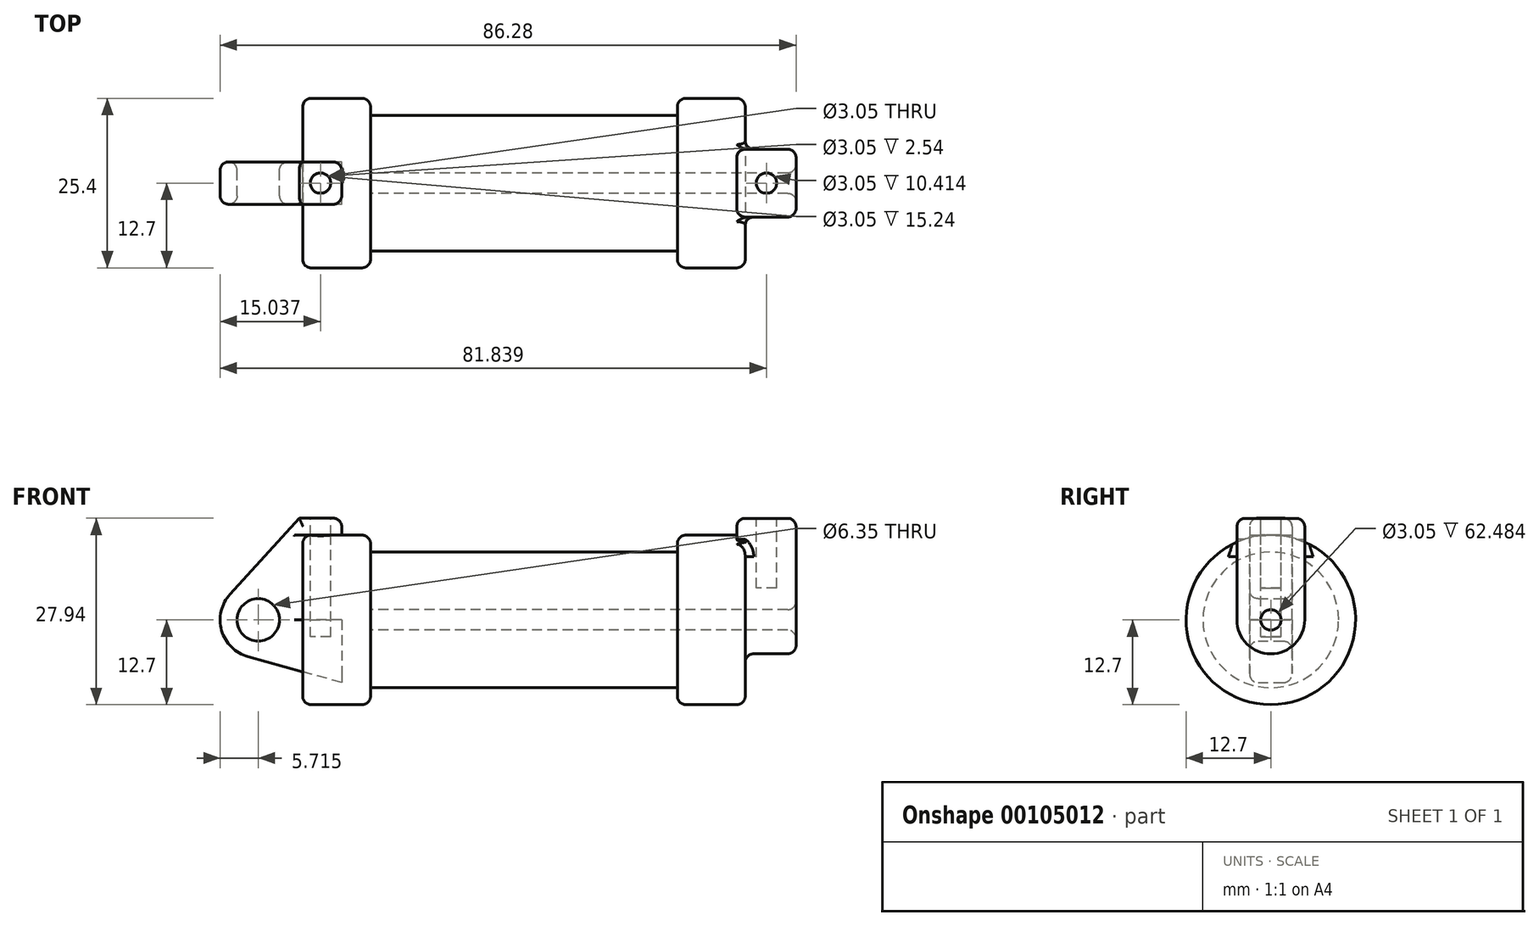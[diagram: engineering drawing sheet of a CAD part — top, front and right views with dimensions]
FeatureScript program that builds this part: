
annotation { "Feature Type Name" : "Feature", "Feature Type Description" : "" }
export const myFeature = defineFeature(function(context is Context, id is Id, definition is map)
    precondition{}
    {
        {
            var Q0;
            Q0=qCreatedBy(makeId("Front.planeOp"),FACE);
            var sketch = newSketch(context, id + "F0", { "sketchPlane" : qUnion([Q0])});
            skLineSegment(sketch, "E0", {"start": v(0, 0) * mm, "end": v(0, 12.7) * mm});
            skLineSegment(sketch, "E1", {"start": v(0, 12.7) * mm, "end": v(10.16, 12.7) * mm});
            skLineSegment(sketch, "E2", {"start": v(10.16, 12.7) * mm, "end": v(10.16, 10.16) * mm});
            skLineSegment(sketch, "E3", {"start": v(10.16, 10.16) * mm, "end": v(56.13, 10.16) * mm});
            skLineSegment(sketch, "E4", {"start": v(56.13, 10.16) * mm, "end": v(56.13, 12.7) * mm});
            skLineSegment(sketch, "E5", {"start": v(56.13, 12.7) * mm, "end": v(66.3, 12.7) * mm});
            skLineSegment(sketch, "E6", {"start": v(66.3, 12.7) * mm, "end": v(66.3, 0) * mm});
            skLineSegment(sketch, "E7", {"start": v(66.3, 0) * mm, "end": v(0, 0) * mm});
            skLineSegment(sketch, "E8", {"start": v(5.84, 15.24) * mm, "end": v(-0.5, 15.24) * mm});
            skLineSegment(sketch, "E9", {"start": v(-0.5, 15.24) * mm, "end": v(-10.88, 3.85) * mm});
            skLineSegment(sketch, "E10", {"start": v(0, 0) * mm, "end": v(-6.65, 0) * mm});
            skCircle(sketch, "E11", {"center": v(-6.65, 0) * mm, "radius": 5.72 * mm});
            skCircle(sketch, "E12", {"center": v(-6.65, 0) * mm, "radius": 3.18 * mm});
            skLineSegment(sketch, "E13", {"start": v(5.84, 15.24) * mm, "end": v(5.84, -9.4) * mm});
            skLineSegment(sketch, "E14", {"start": v(5.84, -9.4) * mm, "end": v(-8.18, -5.5) * mm});
            skSolve(sketch);
        }
        {
            var Q0;
            {var subQ0=sQuery(id+"F0.wireOp",EDGE,"E0");Q0=makeQuery(id+"F0.imprint","IMPRINT",FACE,{"disambiguationData":[TD([[makeQuery(id+"F0.imprint","IMPRINT",EDGE,{"derivedFrom":subQ0}),-1.0]])]});}
            var Q1;
            {var subQ0=sQuery(id+"F0.wireOp",EDGE,"E2");Q1=makeQuery(id+"F0.imprint","IMPRINT",FACE,{"disambiguationData":[TD([[makeQuery(id+"F0.imprint","IMPRINT",EDGE,{"derivedFrom":subQ0}),-1.0]])]});}
            var Q2;
            Q2=sQuery(id+"F0.wireOp",EDGE,"E7");
            revolve(context, id + "F1", {"entities" : qUnion([Q0, Q1]), "axis" : qUnion([Q2]), "revolveType" : RevolveType.FULL});
        }
        {
            var Q0;
            {var subQ3=sQuery(id+"F0.wireOp",EDGE,"E0");Q0=makeQuery(id+"F0.imprint","IMPRINT",FACE,{"disambiguationData":[TD([[makeQuery(id+"F0.imprint","IMPRINT",EDGE,{"derivedFrom":subQ3}),1.0]])]});}
            var Q1;
            {var subQ4=sQuery(id+"F0.wireOp",EDGE,"E12");Q1=makeQuery(id+"F0.imprint","IMPRINT",FACE,{"disambiguationData":[TD([[makeQuery(id+"F0.imprint","IMPRINT",EDGE,{"derivedFrom":subQ4}),-1.0]])]});}
            var Q2;
            {var subQ0=sQuery(id+"F0.wireOp",EDGE,"E14");Q2=makeQuery(id+"F0.imprint","IMPRINT",FACE,{"disambiguationData":[TD([[makeQuery(id+"F0.imprint","IMPRINT",EDGE,{"derivedFrom":subQ0}),-1.0]])]});}
            extrude(context, id + "F2", {"entities" : qUnion([Q0, Q1, Q2]), "endBound" : BoundingType.SYMMETRIC, "depth" : 6.35 * mm});
        }
        {
            var Q0;
            Q0=makeQuery(id+"F1.opRevolve","SWEPT_FACE",FACE,{"disambiguationData":[OSD([sQuery(id+"F0.wireOp",EDGE,"E6")])]});
            var sketch = newSketch(context, id + "F3", { "sketchPlane" : qUnion([Q0])});
            skCircle(sketch, "E15", {"center": v(0, 0) * mm, "radius": 5.08 * mm});
            skCircle(sketch, "E16", {"center": v(0, 0) * mm, "radius": 1.52 * mm});
            skLineSegment(sketch, "E17", {"start": v(-5.08, 0) * mm, "end": v(-5.08, 15.21) * mm});
            skLineSegment(sketch, "E18", {"start": v(5.08, 0) * mm, "end": v(5.08, 15.21) * mm});
            skLineSegment(sketch, "E19", {"start": v(-5.08, 15.21) * mm, "end": v(5.08, 15.21) * mm});
            skSolve(sketch);
        }
        {
            var Q0;
            {var subQ0=sQuery(id+"F3.wireOp",EDGE,"E19");Q0=makeQuery(id+"F3.imprint","IMPRINT",FACE,{"disambiguationData":[TD([[makeQuery(id+"F3.imprint","IMPRINT",EDGE,{"derivedFrom":subQ0}),-1.0]])]});}
            var Q1;
            {var subQ0=sQuery(id+"F3.wireOp",EDGE,"E17");var subQ1=sQuery(id+"F3.wireOp",EDGE,"E15");var subQ2=makeQuery(id+"F3.imprint","INTERSECT",VERTEX,{"derivedFrom":[subQ1,subQ0]});Q1=makeQuery(id+"F3.imprint","IMPRINT",FACE,{"disambiguationData":[TD([[makeQuery(id+"F3.imprint","IMPRINT",EDGE,{"disambiguationData":[TD([[subQ2,1.0]])],"derivedFrom":subQ1}),-1.0]])]});}
            var Q2;
            Q2=makeQuery(id+"F3.imprint","IMPRINT",FACE,{"disambiguationData":[TD([[makeQuery(id+"F3.imprint","IMPRINT",EDGE,{"derivedFrom":sQuery(id+"F3.wireOp",EDGE,"E16")}),-1.0]])]});
            extrude(context, id + "F4", {"entities" : qUnion([Q0, Q1, Q2]), "operationType" : NewBodyOperationType.ADD, "depth" : 7.62 * mm});
        }
        {
            var Q0;
            Q0=makeQuery(id+"F4.opExtrude","CAP_FACE",FACE,{"disambiguationData":[OSD([sQuery(id+"F3.wireOp",EDGE,"E15"),sQuery(id+"F3.wireOp",EDGE,"E16"),sQuery(id+"F3.wireOp",EDGE,"E17"),sQuery(id+"F3.wireOp",EDGE,"E18"),sQuery(id+"F3.wireOp",EDGE,"E19")])],"isStart":true});
            extrude(context, id + "F5", {"entities" : qUnion([Q0]), "operationType" : NewBodyOperationType.ADD, "depth" : 1.27 * mm});
        }
        {
            var Q0;
            Q0=makeQuery(id+"F4.boolean.opBoolean","SPLIT",FACE,{"disambiguationData":[TD([makeQuery(id+"F4.opExtrude","SWEPT_FACE",FACE,{"disambiguationData":[OSD([sQuery(id+"F3.wireOp",EDGE,"E16")])]})])],"derivedFrom":makeQuery(id+"F1.opRevolve","SWEPT_FACE",FACE,{"disambiguationData":[OSD([sQuery(id+"F0.wireOp",EDGE,"E6")])]})});
            var Q1;
            Q1=makeQuery(id+"F1.opRevolve","SWEPT_FACE",FACE,{"disambiguationData":[OSD([sQuery(id+"F0.wireOp",EDGE,"E2")])]});
            extrude(context, id + "F6", {"entities" : qUnion([Q0]), "operationType" : NewBodyOperationType.REMOVE, "endBound" : BoundingType.UP_TO_SURFACE, "oppositeDirection" : true, "endBoundEntityFace" : qUnion([Q1]), "depth" : 25.4 * mm});
        }
        {
            var Q0;
            {var subQ0=sQuery(id+"F3.wireOp",EDGE,"E19");Q0=makeQuery(id+"F5.boolean.opBoolean","MERGE",FACE,{"derivedFrom":[makeQuery(id+"F4.opExtrude","SWEPT_FACE",FACE,{"disambiguationData":[OSD([subQ0])]}),makeQuery(id+"F5.opExtrude","SWEPT_FACE",FACE,{"disambiguationData":[OSD([subQ0])]})]});}
            var sketch = newSketch(context, id + "F7", { "sketchPlane" : qUnion([Q0])});
            skPoint(sketch, "E20.centerSnap0", {"position": v(65.02, 0) * mm});
            skLineSegment(sketch, "E21", {"start": v(69.47, 5.08) * mm, "end": v(69.47, -5.08) * mm, "construction": true});
            skLineSegment(sketch, "E22", {"start": v(65.02, 0) * mm, "end": v(73.91, 0) * mm, "construction": true});
            skCircle(sketch, "E23", {"center": v(69.47, 0) * mm, "radius": 1.52 * mm});
            skSolve(sketch);
        }
        {
            var Q0;
            Q0=makeQuery(id+"F7.imprint","IMPRINT",FACE,{"disambiguationData":[TD([[makeQuery(id+"F7.imprint","IMPRINT",EDGE,{"derivedFrom":sQuery(id+"F7.wireOp",EDGE,"E23")}),1.0]])]});
            var Q1;
            Q1=sQuery(id+"F7.wireOp",EDGE,"E23");
            extrude(context, id + "F8", {"entities" : qUnion([Q0]), "operationType" : NewBodyOperationType.REMOVE, "surfaceEntities" : qUnion([Q1]), "oppositeDirection" : true, "depth" : 10.4 * mm});
        }
        {
            var Q0;
            Q0=makeQuery(id+"F2.opExtrude","SWEPT_FACE",FACE,{"disambiguationData":[OSD([sQuery(id+"F0.wireOp",EDGE,"E8")])]});
            var sketch = newSketch(context, id + "F9", { "sketchPlane" : qUnion([Q0])});
            skLineSegment(sketch, "E24", {"start": v(-0.5, 0) * mm, "end": v(5.84, 0) * mm, "construction": true});
            skLineSegment(sketch, "E25", {"start": v(2.67, 3.18) * mm, "end": v(2.67, -3.18) * mm, "construction": true});
            skCircle(sketch, "E26", {"center": v(2.67, 0) * mm, "radius": 1.52 * mm});
            skSolve(sketch);
        }
        {
            var Q0;
            Q0 = qSketchRegion(id + "F9", true);
            extrude(context, id + "F10", {"entities" : qUnion([Q0]), "operationType" : NewBodyOperationType.REMOVE, "oppositeDirection" : true, "depth" : 17.78 * mm});
        }
        {
            var Q0;
            Q0=makeQuery(id+"F1.opRevolve","SWEPT_EDGE",EDGE,{"disambiguationData":[OSD([sQuery(id+"F0.wireOp",EDGE,"E0"),sQuery(id+"F0.wireOp",EDGE,"E1")])]});
            var Q1;
            Q1=makeQuery(id+"F1.opRevolve","SWEPT_EDGE",EDGE,{"disambiguationData":[OSD([sQuery(id+"F0.wireOp",EDGE,"E1"),sQuery(id+"F0.wireOp",EDGE,"E2")])]});
            var Q2;
            Q2=makeQuery(id+"F1.opRevolve","SWEPT_EDGE",EDGE,{"disambiguationData":[OSD([sQuery(id+"F0.wireOp",EDGE,"E4"),sQuery(id+"F0.wireOp",EDGE,"E5")])]});
            var Q3;
            Q3=makeQuery(id+"F4.boolean.opBoolean","SPLIT",EDGE,{"disambiguationData":[OD(1.0)],"derivedFrom":makeQuery(id+"F1.opRevolve","SWEPT_EDGE",EDGE,{"disambiguationData":[OSD([sQuery(id+"F0.wireOp",EDGE,"E5"),sQuery(id+"F0.wireOp",EDGE,"E6")])]})});
            var Q4;
            Q4=makeQuery(id+"F8.boolean.opBoolean","COPY",EDGE,{"derivedFrom":makeQuery(id+"F8.opExtrude","CAP_EDGE",EDGE,{"disambiguationData":[OSD([sQuery(id+"F7.wireOp",EDGE,"E23")])],"isStart":true})});
            var Q5;
            Q5=makeQuery(id+"F4.opExtrude","CAP_EDGE",EDGE,{"disambiguationData":[OSD([sQuery(id+"F3.wireOp",EDGE,"E16")])],"isStart":false});
            var Q6;
            Q6=makeQuery(id+"F4.opExtrude","CAP_EDGE",EDGE,{"disambiguationData":[OSD([sQuery(id+"F3.wireOp",EDGE,"E17")])],"isStart":false});
            var Q7;
            {var subQ0=sQuery(id+"F3.wireOp",EDGE,"E19");var subQ1=sQuery(id+"F3.wireOp",EDGE,"E17");Q7=makeQuery(id+"F5.boolean.opBoolean","MERGE",EDGE,{"derivedFrom":[makeQuery(id+"F4.opExtrude","SWEPT_EDGE",EDGE,{"disambiguationData":[OSD([subQ1,subQ0])]}),makeQuery(id+"F5.opExtrude","SWEPT_EDGE",EDGE,{"disambiguationData":[OSD([subQ1,subQ0])]})]});}
            var Q8;
            Q8=makeQuery(id+"F4.opExtrude","CAP_EDGE",EDGE,{"disambiguationData":[OSD([sQuery(id+"F3.wireOp",EDGE,"E19")])],"isStart":false});
            var Q9;
            {var subQ0=sQuery(id+"F3.wireOp",EDGE,"E19");var subQ1=sQuery(id+"F3.wireOp",EDGE,"E18");Q9=makeQuery(id+"F5.boolean.opBoolean","MERGE",EDGE,{"derivedFrom":[makeQuery(id+"F4.opExtrude","SWEPT_EDGE",EDGE,{"disambiguationData":[OSD([subQ1,subQ0])]}),makeQuery(id+"F5.opExtrude","SWEPT_EDGE",EDGE,{"disambiguationData":[OSD([subQ1,subQ0])]})]});}
            var Q10;
            Q10=makeQuery(id+"F5.opExtrude","CAP_EDGE",EDGE,{"disambiguationData":[OSD([sQuery(id+"F3.wireOp",EDGE,"E19")])],"isStart":false});
            var Q11;
            Q11=makeQuery(id+"F2.opExtrude","CAP_EDGE",EDGE,{"disambiguationData":[OSD([sQuery(id+"F0.wireOp",EDGE,"E8")])],"isStart":true});
            var Q12;
            Q12=makeQuery(id+"F2.opExtrude","SWEPT_EDGE",EDGE,{"disambiguationData":[OSD([sQuery(id+"F0.wireOp",EDGE,"E8"),sQuery(id+"F0.wireOp",EDGE,"E13")])]});
            var Q13;
            Q13=makeQuery(id+"F2.opExtrude","CAP_EDGE",EDGE,{"disambiguationData":[OSD([sQuery(id+"F0.wireOp",EDGE,"E8")])],"isStart":false});
            var Q14;
            Q14=makeQuery(id+"F10.boolean.opBoolean","COPY",EDGE,{"derivedFrom":makeQuery(id+"F10.opExtrude","CAP_EDGE",EDGE,{"disambiguationData":[OSD([sQuery(id+"F9.wireOp",EDGE,"E26")])],"isStart":true})});
            var Q15;
            Q15=makeQuery(id+"F2.opExtrude","CAP_EDGE",EDGE,{"disambiguationData":[OSD([sQuery(id+"F0.wireOp",EDGE,"E11")])],"isStart":true});
            var Q16;
            Q16=makeQuery(id+"F2.opExtrude","CAP_EDGE",EDGE,{"disambiguationData":[OSD([sQuery(id+"F0.wireOp",EDGE,"E11")])],"isStart":false});
            var Q17;
            Q17=makeQuery(id+"F2.opExtrude","CAP_EDGE",EDGE,{"disambiguationData":[OSD([sQuery(id+"F0.wireOp",EDGE,"E12")])],"isStart":false});
            var Q18;
            Q18=makeQuery(id+"F2.opExtrude","CAP_EDGE",EDGE,{"disambiguationData":[OSD([sQuery(id+"F0.wireOp",EDGE,"E12")])],"isStart":true});
            fillet(context, id + "F11", {"entities" : qUnion([Q0, Q1, Q2, Q3, Q4, Q5, Q6, Q7, Q8, Q9, Q10, Q11, Q12, Q13, Q14, Q15, Q16, Q17, Q18]), "radius" : 1.27 * mm, "tangentPropagation" : true, "allowEdgeOverflow" : false});
        }
        {
            var Q0;
            {var subQ0=sQuery(id+"F3.wireOp",EDGE,"E17");var subQ1=sQuery(id+"F3.wireOp",EDGE,"E15");Q0=makeQuery(id+"F4.boolean.opBoolean","SPLIT",EDGE,{"disambiguationData":[TD([makeQuery(id+"F4.opExtrude","SWEPT_FACE",FACE,{"disambiguationData":[OSD([subQ1])]})])],"derivedFrom":makeQuery(id+"F4.opExtrude","CAP_EDGE",EDGE,{"disambiguationData":[OSD([subQ0])],"isStart":true})});}
            var Q1;
            Q1=makeQuery(id+"F2.opExtrude","CAP_EDGE",EDGE,{"disambiguationData":[OSD([sQuery(id+"F0.wireOp",EDGE,"E0")])],"isStart":false});
            var Q2;
            Q2=makeQuery(id+"F2.opExtrude","CAP_EDGE",EDGE,{"disambiguationData":[OSD([sQuery(id+"F0.wireOp",EDGE,"E0")])],"isStart":true});
            fillet(context, id + "F12", {"entities" : qUnion([Q0, Q1, Q2]), "radius" : 1.27 * mm, "tangentPropagation" : true, "allowEdgeOverflow" : false});
        }
        {
            var Q0;
            Q0=makeQuery(id+"F5.opExtrude","CAP_EDGE",EDGE,{"disambiguationData":[OSD([sQuery(id+"F3.wireOp",EDGE,"E18")])],"isStart":false});
            var Q1;
            Q1=makeQuery(id+"F5.opExtrude","CAP_EDGE",EDGE,{"disambiguationData":[OSD([sQuery(id+"F3.wireOp",EDGE,"E17")])],"isStart":false});
            var Q2;
            {var subQ0=sQuery(id+"F0.wireOp",EDGE,"E13");Q2=makeQuery(id+"F2.opExtrude","CAP_EDGE",EDGE,{"disambiguationData":[OSD([subQ0]),TDD([makeQuery(id+"F0.imprint","IMPRINT",EDGE,{"disambiguationData":[TD([[makeQuery(id+"F0.imprint","INTERSECT",VERTEX,{"derivedFrom":[sQuery(id+"F0.wireOp",EDGE,"E8"),subQ0]}),-1.0]])],"derivedFrom":subQ0})])],"isStart":false});}
            var Q3;
            {var subQ0=sQuery(id+"F0.wireOp",EDGE,"E13");Q3=makeQuery(id+"F2.opExtrude","CAP_EDGE",EDGE,{"disambiguationData":[OSD([subQ0]),TDD([makeQuery(id+"F0.imprint","IMPRINT",EDGE,{"disambiguationData":[TD([[makeQuery(id+"F0.imprint","INTERSECT",VERTEX,{"derivedFrom":[sQuery(id+"F0.wireOp",EDGE,"E8"),subQ0]}),-1.0]])],"derivedFrom":subQ0})])],"isStart":true});}
            fillet(context, id + "F13", {"entities" : qUnion([Q0, Q1, Q2, Q3]), "radius" : 1.27 * mm, "tangentPropagation" : true, "allowEdgeOverflow" : false});
        }
    });
